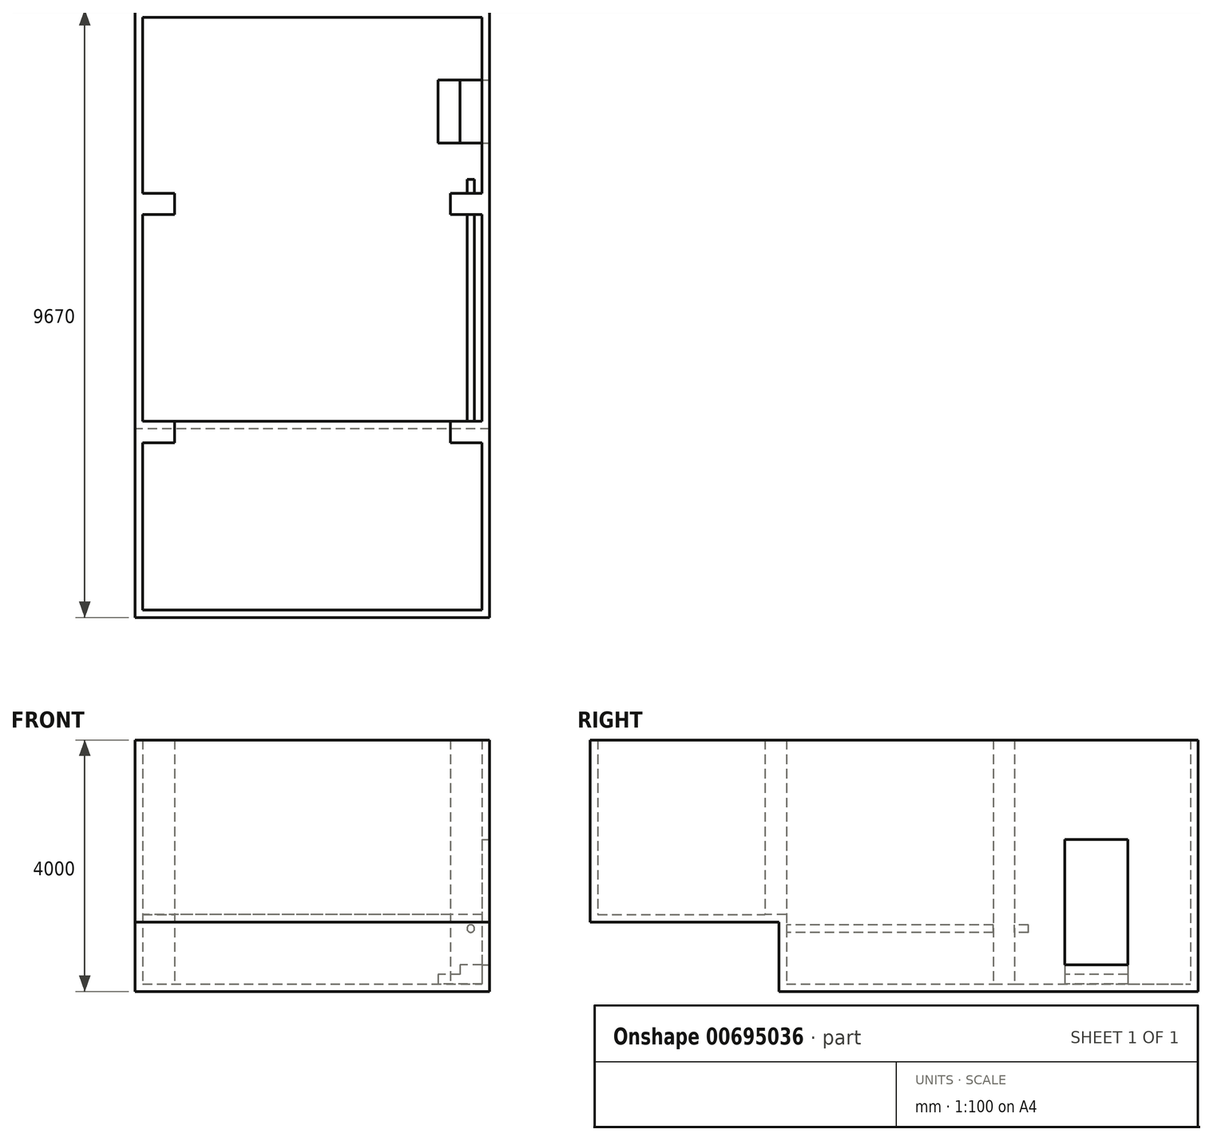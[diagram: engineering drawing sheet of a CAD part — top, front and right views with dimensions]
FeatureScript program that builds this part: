
annotation { "Feature Type Name" : "Feature", "Feature Type Description" : "" }
export const myFeature = defineFeature(function(context is Context, id is Id, definition is map)
    precondition{}
    {
        {
            var Q0;
            Q0=qCreatedBy(makeId("Top.planeOp"),FACE);
            var sketch = newSketch(context, id + "F0", { "sketchPlane" : qUnion([Q0])});
            skLineSegment(sketch, "E0.bottom", {"start": v(-7275.77, 0) * mm, "end": v(-1635.77, 0) * mm});
            skLineSegment(sketch, "E0.top", {"start": v(-7275.77, 6670) * mm, "end": v(-1635.77, 6670) * mm});
            skLineSegment(sketch, "E0.left", {"start": v(-7275.77, 0) * mm, "end": v(-7275.77, 6670) * mm});
            skLineSegment(sketch, "E0.right", {"start": v(-1635.77, 0) * mm, "end": v(-1635.77, 6670) * mm});
            skSolve(sketch);
        }
        {
            var Q0;
            Q0 = qSketchRegion(id + "F0", true);
            extrude(context, id + "F1", {"entities" : qUnion([Q0]), "depth" : 4000 * mm, "offsetDistance" : 25 * mm});
        }
        {
            var Q0;
            Q0=makeQuery(id+"F1.opExtrude","SWEPT_FACE",FACE,{"disambiguationData":[OSD([sQuery(id+"F0.wireOp",EDGE,"E0.bottom")])]});
            var sketch = newSketch(context, id + "F2", { "sketchPlane" : qUnion([Q0])});
            skLineSegment(sketch, "E1.top", {"start": v(-1635.77, 1100) * mm, "end": v(-7275.77, 1100) * mm});
            skLineSegment(sketch, "E2.bottom", {"start": v(-1635.77, 4000) * mm, "end": v(-7275.77, 4000) * mm});
            skLineSegment(sketch, "E2.left", {"start": v(-1635.77, 4000) * mm, "end": v(-1635.77, 1100) * mm});
            skLineSegment(sketch, "E2.right", {"start": v(-7275.77, 4000) * mm, "end": v(-7275.77, 1100) * mm});
            skSolve(sketch);
        }
        {
            var Q0;
            Q0=makeQuery(id+"F2.imprint","IMPRINT",FACE,{"disambiguationData":[TD([[makeQuery(id+"F2.imprint","IMPRINT",EDGE,{"derivedFrom":sQuery(id+"F2.wireOp",EDGE,"E1.top")}),-1.0]])]});
            extrude(context, id + "F3", {"entities" : qUnion([Q0]), "operationType" : NewBodyOperationType.ADD, "depth" : 3000 * mm, "offsetDistance" : 25 * mm});
        }
        {
            var Q0;
            Q0=makeQuery(id+"F3.boolean.opBoolean","MERGE",FACE,{"derivedFrom":[makeQuery(id+"F1.opExtrude","CAP_FACE",FACE,{"disambiguationData":[OSD([sQuery(id+"F0.wireOp",EDGE,"E0.bottom"),sQuery(id+"F0.wireOp",EDGE,"E0.top"),sQuery(id+"F0.wireOp",EDGE,"E0.left"),sQuery(id+"F0.wireOp",EDGE,"E0.right")])],"isStart":false}),makeQuery(id+"F3.opExtrude","SWEPT_FACE",FACE,{"disambiguationData":[OSD([sQuery(id+"F2.wireOp",EDGE,"E2.bottom")])]})]});
            shell(context, id + "F4", {"entities" : qUnion([Q0]), "thickness" : 120 * mm});
        }
        {
            var Q0;
            Q0=makeQuery(id+"F9Hgr0WSP0JQNdl_1.boolean.opBoolean","MERGE",FACE,{"derivedFrom":[makeQuery(id+"F4.opShell","OFFSET_FACE",FACE,{"disambiguationData":[OSD([sQuery(id+"F0.wireOp",EDGE,"E0.bottom"),sQuery(id+"F0.wireOp",EDGE,"E0.top"),sQuery(id+"F0.wireOp",EDGE,"E0.left"),sQuery(id+"F0.wireOp",EDGE,"E0.right")])]}),makeQuery(id+"F9Hgr0WSP0JQNdl_1.opExtrude","SWEPT_FACE",FACE,{"disambiguationData":[OSD([sQuery(id+"FqhZE0eb5RG5OJy_1.wireOp",EDGE,"VNqoOLc0-ISac-aWrl-rsNl-bNCGV65gnAKh.top")])]})]});
            var sketch = newSketch(context, id + "F5", { "sketchPlane" : qUnion([Q0])});
            skLineSegment(sketch, "E3.bottom", {"start": v(-1755.77, 3750) * mm, "end": v(-2260.77, 3750) * mm});
            skLineSegment(sketch, "E3.top", {"start": v(-1755.77, 3410) * mm, "end": v(-2260.77, 3410) * mm});
            skLineSegment(sketch, "E3.left", {"start": v(-1755.77, 3750) * mm, "end": v(-1755.77, 3410) * mm});
            skLineSegment(sketch, "E3.right", {"start": v(-2260.77, 3750) * mm, "end": v(-2260.77, 3410) * mm});
            skLineSegment(sketch, "E4.bottom", {"start": v(-7155.77, 3410) * mm, "end": v(-6650.77, 3410) * mm});
            skLineSegment(sketch, "E4.top", {"start": v(-7155.77, 3750) * mm, "end": v(-6650.77, 3750) * mm});
            skLineSegment(sketch, "E4.left", {"start": v(-7155.77, 3410) * mm, "end": v(-7155.77, 3750) * mm});
            skLineSegment(sketch, "E4.right", {"start": v(-6650.77, 3410) * mm, "end": v(-6650.77, 3750) * mm});
            skSolve(sketch);
        }
        {
            var Q0;
            Q0=makeQuery(id+"F5.imprint","IMPRINT",FACE,{"disambiguationData":[TD([[makeQuery(id+"F5.imprint","IMPRINT",EDGE,{"derivedFrom":sQuery(id+"F5.wireOp",EDGE,"E4.bottom")}),1.0]])]});
            var Q1;
            Q1=makeQuery(id+"F5.imprint","IMPRINT",FACE,{"disambiguationData":[TD([[makeQuery(id+"F5.imprint","IMPRINT",EDGE,{"derivedFrom":sQuery(id+"F5.wireOp",EDGE,"E3.bottom")}),1.0]])]});
            extrude(context, id + "F6", {"entities" : qUnion([Q0, Q1]), "operationType" : NewBodyOperationType.ADD, "depth" : 3880 * mm, "offsetDistance" : 25 * mm});
        }
        {
            var Q0;
            Q0=makeQuery(id+"F4.opShell","OFFSET_FACE",FACE,{"disambiguationData":[OSD([sQuery(id+"F0.wireOp",EDGE,"E0.bottom")])]});
            var sketch = newSketch(context, id + "F7", { "sketchPlane" : qUnion([Q0])});
            skCircle(sketch, "E5", {"center": v(1935.77, 1000) * mm, "radius": 60 * mm});
            skSolve(sketch);
        }
        {
            var Q0;
            Q0=makeQuery(id+"F7.imprint","IMPRINT",FACE,{"disambiguationData":[TD([[makeQuery(id+"F7.imprint","IMPRINT",EDGE,{"derivedFrom":sQuery(id+"F7.wireOp",EDGE,"E5")}),1.0]])]});
            extrude(context, id + "F8", {"entities" : qUnion([Q0]), "operationType" : NewBodyOperationType.ADD, "depth" : 3850 * mm, "offsetDistance" : 25 * mm});
        }
        {
            var Q0;
            Q0=makeQuery(id+"F4.opShell","OFFSET_FACE",FACE,{"disambiguationData":[OSD([sQuery(id+"F0.wireOp",EDGE,"E0.bottom"),sQuery(id+"F0.wireOp",EDGE,"E0.top"),sQuery(id+"F0.wireOp",EDGE,"E0.left"),sQuery(id+"F0.wireOp",EDGE,"E0.right")])]});
            var sketch = newSketch(context, id + "F9", { "sketchPlane" : qUnion([Q0])});
            skLineSegment(sketch, "E6.bottom", {"start": v(-1755.77, 5550) * mm, "end": v(-2455.77, 5550) * mm});
            skLineSegment(sketch, "E6.top", {"start": v(-1755.77, 4550) * mm, "end": v(-2455.77, 4550) * mm});
            skLineSegment(sketch, "E6.left", {"start": v(-1755.77, 5550) * mm, "end": v(-1755.77, 4550) * mm});
            skLineSegment(sketch, "E6.right", {"start": v(-2455.77, 5550) * mm, "end": v(-2455.77, 4550) * mm});
            skLineSegment(sketch, "E7", {"start": v(-2105.77, 5550) * mm, "end": v(-2105.77, 4550) * mm});
            skSolve(sketch);
        }
        {
            var Q0;
            {var subQ0=sQuery(id+"F9.wireOp",EDGE,"E6.left");Q0=makeQuery(id+"F9.imprint","IMPRINT",FACE,{"disambiguationData":[TD([[makeQuery(id+"F9.imprint","IMPRINT",EDGE,{"derivedFrom":subQ0}),1.0]])]});}
            extrude(context, id + "F10", {"entities" : qUnion([Q0]), "operationType" : NewBodyOperationType.ADD, "depth" : 300 * mm, "offsetDistance" : 25 * mm});
        }
        {
            var Q0;
            {var subQ0=sQuery(id+"F9.wireOp",EDGE,"E6.right");Q0=makeQuery(id+"F9.imprint","IMPRINT",FACE,{"disambiguationData":[TD([[makeQuery(id+"F9.imprint","IMPRINT",EDGE,{"derivedFrom":subQ0}),1.0]])]});}
            extrude(context, id + "F11", {"entities" : qUnion([Q0]), "operationType" : NewBodyOperationType.ADD, "depth" : 150 * mm, "offsetDistance" : 25 * mm});
        }
        {
            var Q0;
            Q0=makeQuery(id+"F3.boolean.opBoolean","MERGE",FACE,{"derivedFrom":[makeQuery(id+"F1.opExtrude","SWEPT_FACE",FACE,{"disambiguationData":[OSD([sQuery(id+"F0.wireOp",EDGE,"E0.right")])]}),makeQuery(id+"F3.opExtrude","SWEPT_FACE",FACE,{"disambiguationData":[OSD([sQuery(id+"F2.wireOp",EDGE,"E2.left")])]})]});
            var sketch = newSketch(context, id + "F12", { "sketchPlane" : qUnion([Q0])});
            skLineSegment(sketch, "E8.bottom", {"start": v(4550, 2420) * mm, "end": v(5550, 2420) * mm});
            skLineSegment(sketch, "E8.top", {"start": v(4550, 420) * mm, "end": v(5550, 420) * mm});
            skLineSegment(sketch, "E8.left", {"start": v(4550, 2420) * mm, "end": v(4550, 420) * mm});
            skLineSegment(sketch, "E8.right", {"start": v(5550, 2420) * mm, "end": v(5550, 420) * mm});
            skSolve(sketch);
        }
        {
            var Q0;
            Q0=makeQuery(id+"F12.imprint","IMPRINT",FACE,{"disambiguationData":[TD([[makeQuery(id+"F12.imprint","IMPRINT",EDGE,{"derivedFrom":sQuery(id+"F12.wireOp",EDGE,"E8.bottom")}),-1.0]])]});
            extrude(context, id + "F13", {"entities" : qUnion([Q0]), "operationType" : NewBodyOperationType.REMOVE, "oppositeDirection" : true, "depth" : 120 * mm, "offsetDistance" : 25 * mm});
        }
        {
            var Q0;
            Q0=makeQuery(id+"F4.opShell","OFFSET_FACE",FACE,{"disambiguationData":[OSD([sQuery(id+"F2.wireOp",EDGE,"E1.top")])]});
            var sketch = newSketch(context, id + "F14", { "sketchPlane" : qUnion([Q0])});
            skLineSegment(sketch, "E9.bottom", {"start": v(-1755.77, 120) * mm, "end": v(-2260.77, 120) * mm});
            skLineSegment(sketch, "E9.top", {"start": v(-1755.77, -220) * mm, "end": v(-2260.77, -220) * mm});
            skLineSegment(sketch, "E9.left", {"start": v(-1755.77, 120) * mm, "end": v(-1755.77, -220) * mm});
            skLineSegment(sketch, "E9.right", {"start": v(-2260.77, 120) * mm, "end": v(-2260.77, -220) * mm});
            skLineSegment(sketch, "E10.bottom", {"start": v(-7155.77, 120) * mm, "end": v(-6650.77, 120) * mm});
            skLineSegment(sketch, "E10.top", {"start": v(-7155.77, -220) * mm, "end": v(-6650.77, -220) * mm});
            skLineSegment(sketch, "E10.left", {"start": v(-7155.77, 120) * mm, "end": v(-7155.77, -220) * mm});
            skLineSegment(sketch, "E10.right", {"start": v(-6650.77, 120) * mm, "end": v(-6650.77, -220) * mm});
            skSolve(sketch);
        }
        {
            var Q0;
            Q0=makeQuery(id+"F14.imprint","IMPRINT",FACE,{"disambiguationData":[TD([[makeQuery(id+"F14.imprint","IMPRINT",EDGE,{"derivedFrom":sQuery(id+"F14.wireOp",EDGE,"E9.bottom")}),1.0]])]});
            var Q1;
            Q1=makeQuery(id+"F14.imprint","IMPRINT",FACE,{"disambiguationData":[TD([[makeQuery(id+"F14.imprint","IMPRINT",EDGE,{"derivedFrom":sQuery(id+"F14.wireOp",EDGE,"E10.bottom")}),1.0]])]});
            extrude(context, id + "F15", {"entities" : qUnion([Q0, Q1]), "operationType" : NewBodyOperationType.ADD, "depth" : 2780 * mm, "offsetDistance" : 25 * mm});
        }
    });
